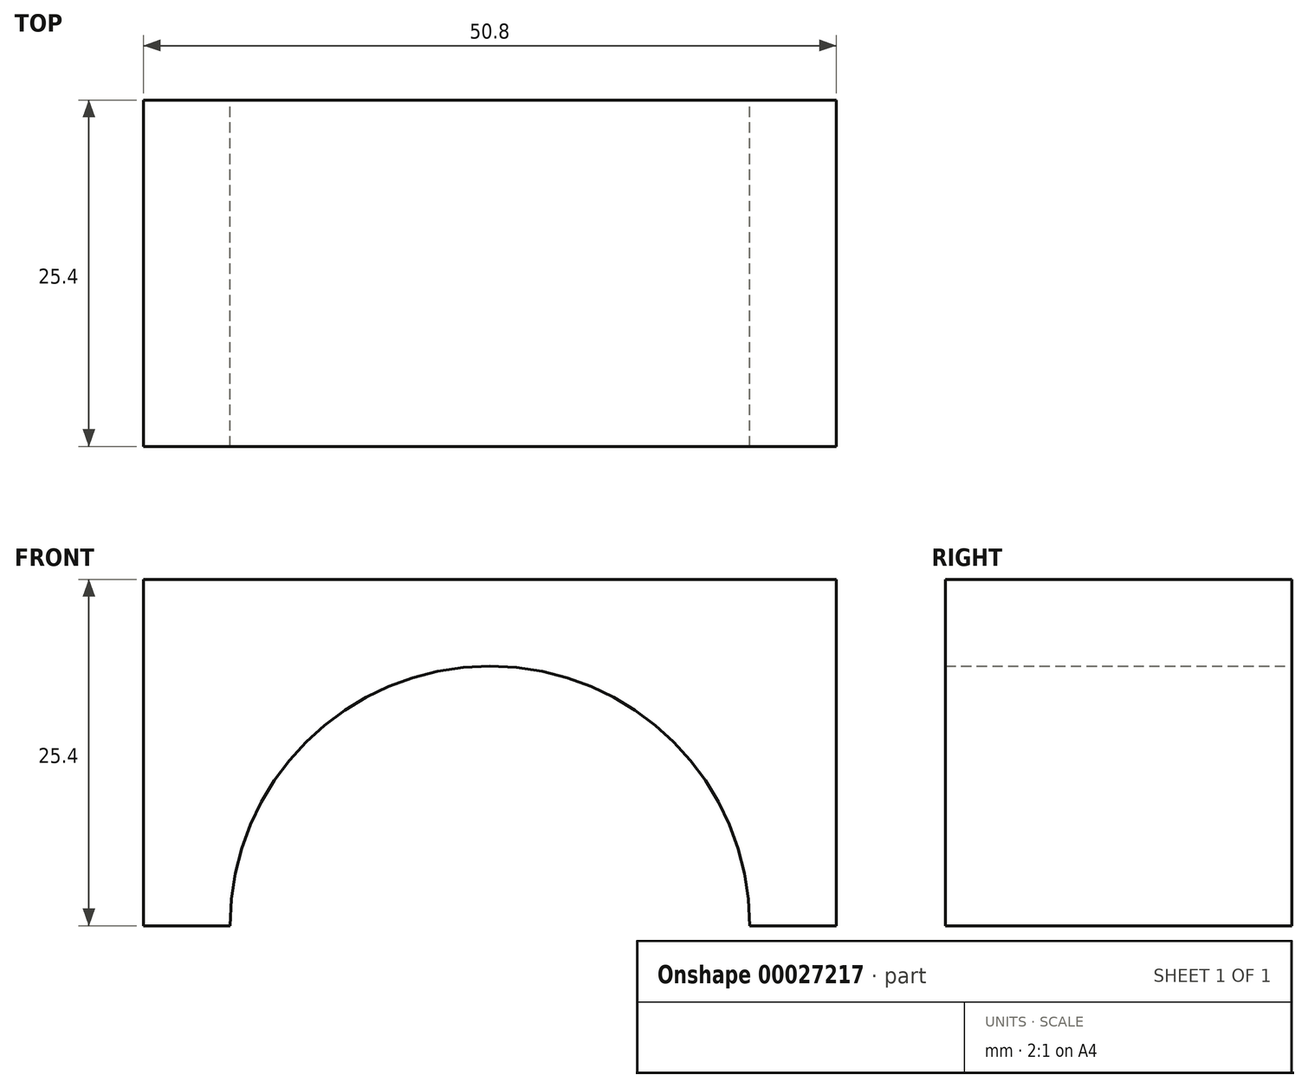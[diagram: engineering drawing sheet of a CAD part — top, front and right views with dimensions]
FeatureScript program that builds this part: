
annotation { "Feature Type Name" : "Feature", "Feature Type Description" : "" }
export const myFeature = defineFeature(function(context is Context, id is Id, definition is map)
    precondition{}
    {
        {
            var Q0;
            Q0=qCreatedBy(makeId("Front.planeOp"),FACE);
            var sketch = newSketch(context, id + "F0", { "sketchPlane" : qUnion([Q0])});
            skLineSegment(sketch, "E0", {"start": v(0, 0) * mm, "end": v(0, 25.4) * mm});
            skLineSegment(sketch, "E1", {"start": v(0, 25.4) * mm, "end": v(50.8, 25.4) * mm});
            skLineSegment(sketch, "E2", {"start": v(50.8, 25.4) * mm, "end": v(50.8, 0) * mm});
            skLineSegment(sketch, "E3", {"start": v(50.8, 0) * mm, "end": v(44.45, 0) * mm});
            skArc(sketch, "E4", {"start": v(44.45, 0) * mm, "mid": v(25.4, 19.05) * mm, "end": v(6.35, 0) * mm});
            skLineSegment(sketch, "E5.trimOffspring", {"start": v(6.35, 0) * mm, "end": v(0, 0) * mm});
            skSolve(sketch);
        }
        {
            var Q0;
            Q0=makeQuery(id+"F0.imprint","IMPRINT",FACE,{"disambiguationData":[TD([[makeQuery(id+"F0.imprint","IMPRINT",EDGE,{"derivedFrom":sQuery(id+"F0.wireOp",EDGE,"E0")}),-1.0]])]});
            extrude(context, id + "F1", {"entities" : qUnion([Q0]), "depth" : 25.4 * mm});
        }
    });
